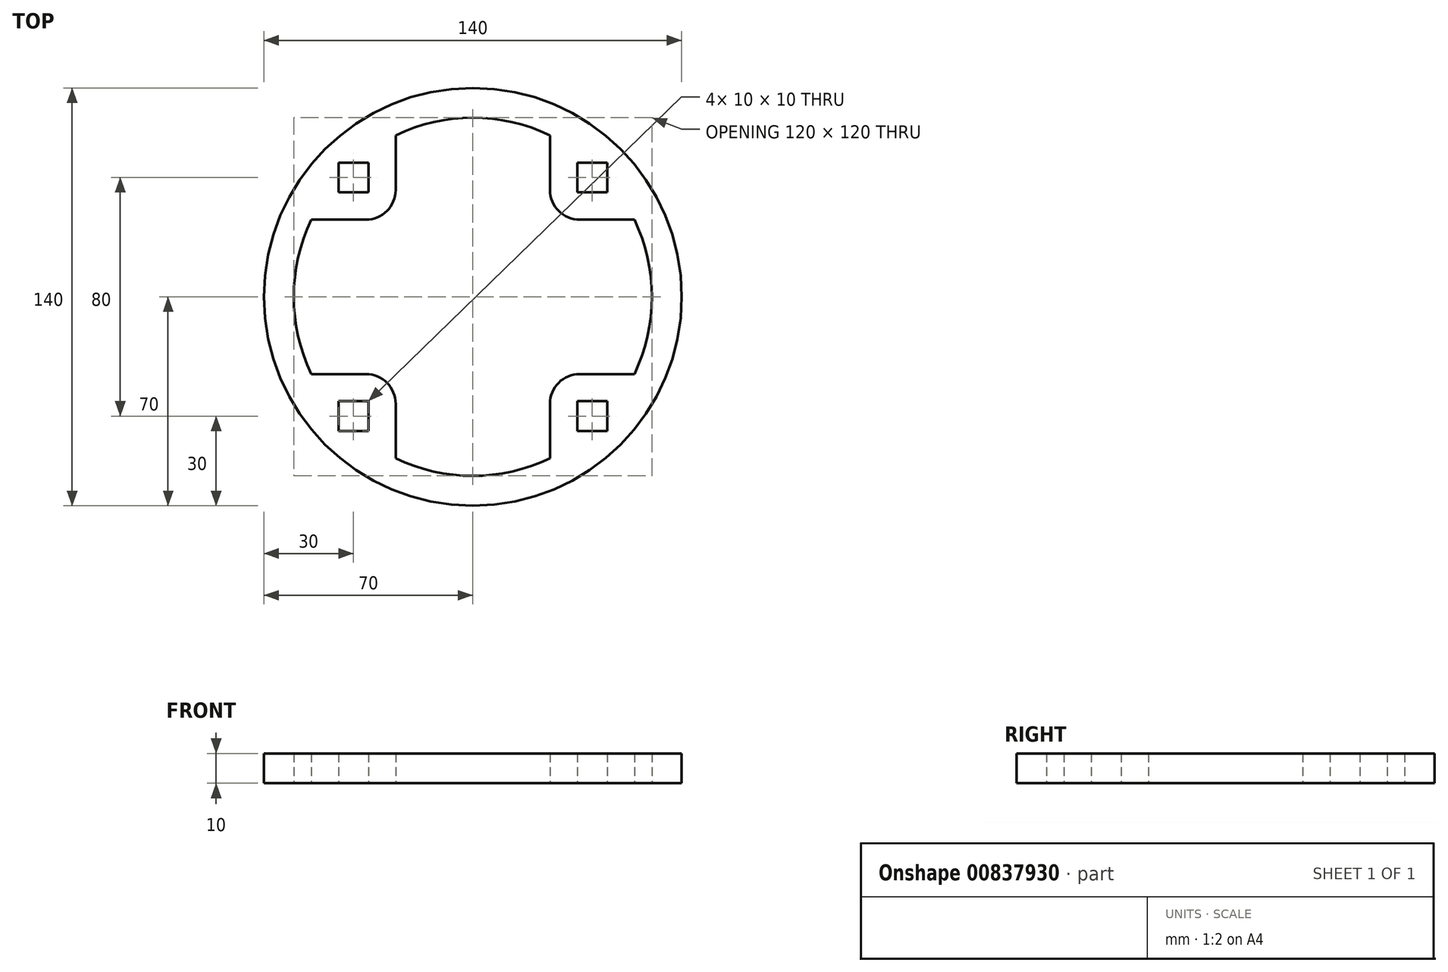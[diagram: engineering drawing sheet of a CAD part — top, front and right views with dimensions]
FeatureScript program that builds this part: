
annotation { "Feature Type Name" : "Feature", "Feature Type Description" : "" }
export const myFeature = defineFeature(function(context is Context, id is Id, definition is map)
    precondition{}
    {
        {
            var Q0;
            Q0=qCreatedBy(makeId("Top.planeOp"),FACE);
            var sketch = newSketch(context, id + "F0", { "sketchPlane" : qUnion([Q0])});
            skCircle(sketch, "E0", {"center": v(0, 0) * mm, "radius": 70 * mm});
            skCircle(sketch, "E1", {"center": v(0, 0) * mm, "radius": 60 * mm});
            skLineSegment(sketch, "E2.bottom", {"start": v(40, 40) * mm, "end": v(-40, 40) * mm});
            skLineSegment(sketch, "E2.top", {"start": v(40, -40) * mm, "end": v(-40, -40) * mm});
            skLineSegment(sketch, "E2.left", {"start": v(40, 40) * mm, "end": v(40, -40) * mm});
            skLineSegment(sketch, "E2.right", {"start": v(-40, 40) * mm, "end": v(-40, -40) * mm});
            skLineSegment(sketch, "E3.bottom", {"start": v(45, 45) * mm, "end": v(35, 45) * mm});
            skLineSegment(sketch, "E3.top", {"start": v(45, 35) * mm, "end": v(35, 35) * mm});
            skLineSegment(sketch, "E3.left", {"start": v(45, 45) * mm, "end": v(45, 35) * mm});
            skLineSegment(sketch, "E3.right", {"start": v(35, 45) * mm, "end": v(35, 35) * mm});
            skPoint(sketch, "E3.middle", {"position": v(40, 40) * mm});
            skLineSegment(sketch, "E4.bottom", {"start": v(54.14, 54.14) * mm, "end": v(25.86, 54.14) * mm});
            skLineSegment(sketch, "E4.top", {"start": v(54.14, 25.86) * mm, "end": v(25.86, 25.86) * mm});
            skLineSegment(sketch, "E4.left", {"start": v(54.14, 54.14) * mm, "end": v(54.14, 25.86) * mm});
            skLineSegment(sketch, "E4.right", {"start": v(25.86, 54.14) * mm, "end": v(25.86, 25.86) * mm});
            skPoint(sketch, "E5.MirrorP", {"position": v(-40, 40) * mm});
            skLineSegment(sketch, "E6.MirrorCS", {"start": v(-45, 45) * mm, "end": v(-45, 35) * mm});
            skLineSegment(sketch, "E7.MirrorCS", {"start": v(-54.14, 54.14) * mm, "end": v(-25.86, 54.14) * mm});
            skLineSegment(sketch, "E8.MirrorCS", {"start": v(-54.14, 54.14) * mm, "end": v(-54.14, 25.86) * mm});
            skLineSegment(sketch, "E9.MirrorCS", {"start": v(-45, 35) * mm, "end": v(-35, 35) * mm});
            skLineSegment(sketch, "E10.MirrorCS", {"start": v(-25.86, 54.14) * mm, "end": v(-25.86, 25.86) * mm});
            skLineSegment(sketch, "E11.MirrorCS", {"start": v(-45, 45) * mm, "end": v(-35, 45) * mm});
            skLineSegment(sketch, "E12.MirrorCS", {"start": v(-54.14, 25.86) * mm, "end": v(-25.86, 25.86) * mm});
            skLineSegment(sketch, "E13.MirrorCS", {"start": v(-35, 45) * mm, "end": v(-35, 35) * mm});
            skLineSegment(sketch, "E14.MirrorCS", {"start": v(-40, 40) * mm, "end": v(40, 40) * mm});
            skPoint(sketch, "E15.MirrorP", {"position": v(-40, -40) * mm});
            skLineSegment(sketch, "E16.MirrorCS", {"start": v(-45, -45) * mm, "end": v(-45, -35) * mm});
            skLineSegment(sketch, "E17.MirrorCS", {"start": v(-54.14, -25.86) * mm, "end": v(-25.86, -25.86) * mm});
            skLineSegment(sketch, "E18.MirrorCS", {"start": v(-54.14, -54.14) * mm, "end": v(-25.86, -54.14) * mm});
            skLineSegment(sketch, "E19.MirrorCS", {"start": v(-45, -35) * mm, "end": v(-35, -35) * mm});
            skLineSegment(sketch, "E20.MirrorCS", {"start": v(-45, -45) * mm, "end": v(-35, -45) * mm});
            skLineSegment(sketch, "E21.MirrorCS", {"start": v(-25.86, -54.14) * mm, "end": v(-25.86, -25.86) * mm});
            skLineSegment(sketch, "E22.MirrorCS", {"start": v(-35, -45) * mm, "end": v(-35, -35) * mm});
            skLineSegment(sketch, "E23.MirrorCS", {"start": v(-54.14, -54.14) * mm, "end": v(-54.14, -25.86) * mm});
            skPoint(sketch, "E24.MirrorP", {"position": v(40, -40) * mm});
            skLineSegment(sketch, "E25.MirrorCS", {"start": v(45, -35) * mm, "end": v(35, -35) * mm});
            skLineSegment(sketch, "E26.MirrorCS", {"start": v(54.14, -25.86) * mm, "end": v(25.86, -25.86) * mm});
            skLineSegment(sketch, "E27.MirrorCS", {"start": v(45, -45) * mm, "end": v(35, -45) * mm});
            skLineSegment(sketch, "E28.MirrorCS", {"start": v(25.86, -54.14) * mm, "end": v(25.86, -25.86) * mm});
            skLineSegment(sketch, "E29.MirrorCS", {"start": v(45, -45) * mm, "end": v(45, -35) * mm});
            skLineSegment(sketch, "E30.MirrorCS", {"start": v(54.14, -54.14) * mm, "end": v(25.86, -54.14) * mm});
            skLineSegment(sketch, "E31.MirrorCS", {"start": v(35, -45) * mm, "end": v(35, -35) * mm});
            skLineSegment(sketch, "E32.MirrorCS", {"start": v(54.14, -54.14) * mm, "end": v(54.14, -25.86) * mm});
            skSolve(sketch);
        }
        {
            var Q0;
            {var subQ0=sQuery(id+"F0.wireOp",EDGE,"E8.MirrorCS");var subQ1=sQuery(id+"F0.wireOp",EDGE,"E0");var subQ2=makeQuery(id+"F0.imprint","INTERSECT",VERTEX,{"derivedFrom":[subQ1,subQ0]});Q0=makeQuery(id+"F0.imprint","IMPRINT",FACE,{"disambiguationData":[TD([[makeQuery(id+"F0.imprint","IMPRINT",EDGE,{"disambiguationData":[TD([[subQ2,-1.0]])],"derivedFrom":subQ1}),1.0]])]});}
            var Q1;
            {var subQ8=sQuery(id+"F0.wireOp",EDGE,"E0");var subQ10=sQuery(id+"F0.wireOp",EDGE,"E7.MirrorCS");var subQ12=makeQuery(id+"F0.imprint","INTERSECT",VERTEX,{"derivedFrom":[subQ8,subQ10]});Q1=makeQuery(id+"F0.imprint","IMPRINT",FACE,{"disambiguationData":[TD([[makeQuery(id+"F0.imprint","IMPRINT",EDGE,{"disambiguationData":[TD([[subQ12,-1.0]])],"derivedFrom":subQ8}),1.0]])]});}
            var Q2;
            {var subQ0=sQuery(id+"F0.wireOp",EDGE,"E4.bottom");var subQ1=sQuery(id+"F0.wireOp",EDGE,"E0");var subQ2=makeQuery(id+"F0.imprint","INTERSECT",VERTEX,{"derivedFrom":[subQ1,subQ0]});Q2=makeQuery(id+"F0.imprint","IMPRINT",FACE,{"disambiguationData":[TD([[makeQuery(id+"F0.imprint","IMPRINT",EDGE,{"disambiguationData":[TD([[subQ2,-1.0]])],"derivedFrom":subQ1}),1.0]])]});}
            var Q3;
            {var subQ3=sQuery(id+"F0.wireOp",EDGE,"E0");var subQ7=sQuery(id+"F0.wireOp",EDGE,"E4.bottom");var subQ9=makeQuery(id+"F0.imprint","INTERSECT",VERTEX,{"derivedFrom":[subQ3,subQ7]});Q3=makeQuery(id+"F0.imprint","IMPRINT",FACE,{"disambiguationData":[TD([[makeQuery(id+"F0.imprint","IMPRINT",EDGE,{"disambiguationData":[TD([[subQ9,1.0]])],"derivedFrom":subQ3}),1.0]])]});}
            var Q4;
            {var subQ0=sQuery(id+"F0.wireOp",EDGE,"E4.left");var subQ1=sQuery(id+"F0.wireOp",EDGE,"E0");var subQ2=makeQuery(id+"F0.imprint","INTERSECT",VERTEX,{"derivedFrom":[subQ1,subQ0]});Q4=makeQuery(id+"F0.imprint","IMPRINT",FACE,{"disambiguationData":[TD([[makeQuery(id+"F0.imprint","IMPRINT",EDGE,{"disambiguationData":[TD([[subQ2,1.0]])],"derivedFrom":subQ1}),1.0]])]});}
            var Q5;
            {var subQ5=sQuery(id+"F0.wireOp",EDGE,"E30.MirrorCS");var subQ10=sQuery(id+"F0.wireOp",EDGE,"E0");var subQ11=makeQuery(id+"F0.imprint","INTERSECT",VERTEX,{"derivedFrom":[subQ10,subQ5]});Q5=makeQuery(id+"F0.imprint","IMPRINT",FACE,{"disambiguationData":[TD([[makeQuery(id+"F0.imprint","IMPRINT",EDGE,{"disambiguationData":[TD([[subQ11,-1.0]])],"derivedFrom":subQ10}),1.0]])]});}
            var Q6;
            {var subQ0=sQuery(id+"F0.wireOp",EDGE,"E18.MirrorCS");var subQ1=sQuery(id+"F0.wireOp",EDGE,"E0");var subQ2=makeQuery(id+"F0.imprint","INTERSECT",VERTEX,{"derivedFrom":[subQ1,subQ0]});Q6=makeQuery(id+"F0.imprint","IMPRINT",FACE,{"disambiguationData":[TD([[makeQuery(id+"F0.imprint","IMPRINT",EDGE,{"disambiguationData":[TD([[subQ2,-1.0]])],"derivedFrom":subQ1}),1.0]])]});}
            var Q7;
            {var subQ8=sQuery(id+"F0.wireOp",EDGE,"E23.MirrorCS");var subQ10=sQuery(id+"F0.wireOp",EDGE,"E0");var subQ11=makeQuery(id+"F0.imprint","INTERSECT",VERTEX,{"derivedFrom":[subQ10,subQ8]});Q7=makeQuery(id+"F0.imprint","IMPRINT",FACE,{"disambiguationData":[TD([[makeQuery(id+"F0.imprint","IMPRINT",EDGE,{"disambiguationData":[TD([[subQ11,-1.0]])],"derivedFrom":subQ10}),1.0]])]});}
            var Q8;
            {var subQ0=sQuery(id+"F0.wireOp",EDGE,"E21.MirrorCS");var subQ8=sQuery(id+"F0.wireOp",EDGE,"E2.top");var subQ11=makeQuery(id+"F0.imprint","INTERSECT",VERTEX,{"derivedFrom":[subQ8,subQ0]});Q8=makeQuery(id+"F0.imprint","IMPRINT",FACE,{"disambiguationData":[TD([[makeQuery(id+"F0.imprint","IMPRINT",EDGE,{"disambiguationData":[TD([[subQ11,-1.0]])],"derivedFrom":subQ8}),-1.0]])]});}
            var Q9;
            {var subQ0=sQuery(id+"F0.wireOp",EDGE,"E17.MirrorCS");var subQ3=sQuery(id+"F0.wireOp",EDGE,"E2.right");var subQ4=makeQuery(id+"F0.imprint","INTERSECT",VERTEX,{"derivedFrom":[subQ3,subQ0]});Q9=makeQuery(id+"F0.imprint","IMPRINT",FACE,{"disambiguationData":[TD([[makeQuery(id+"F0.imprint","IMPRINT",EDGE,{"disambiguationData":[TD([[subQ4,-1.0]])],"derivedFrom":subQ3}),-1.0]])]});}
            var Q10;
            {var subQ5=sQuery(id+"F0.wireOp",EDGE,"E2.top");var subQ7=sQuery(id+"F0.wireOp",EDGE,"E21.MirrorCS");var subQ8=makeQuery(id+"F0.imprint","INTERSECT",VERTEX,{"derivedFrom":[subQ5,subQ7]});Q10=makeQuery(id+"F0.imprint","IMPRINT",FACE,{"disambiguationData":[TD([[makeQuery(id+"F0.imprint","IMPRINT",EDGE,{"disambiguationData":[TD([[subQ8,-1.0]])],"derivedFrom":subQ5}),1.0]])]});}
            var Q11;
            {var subQ0=sQuery(id+"F0.wireOp",EDGE,"E31.MirrorCS");var subQ7=sQuery(id+"F0.wireOp",EDGE,"E2.top");var subQ9=makeQuery(id+"F0.imprint","INTERSECT",VERTEX,{"derivedFrom":[subQ7,subQ0]});Q11=makeQuery(id+"F0.imprint","IMPRINT",FACE,{"disambiguationData":[TD([[makeQuery(id+"F0.imprint","IMPRINT",EDGE,{"disambiguationData":[TD([[subQ9,-1.0]])],"derivedFrom":subQ7}),1.0]])]});}
            var Q12;
            {var subQ7=sQuery(id+"F0.wireOp",EDGE,"E2.top");var subQ9=sQuery(id+"F0.wireOp",EDGE,"E31.MirrorCS");var subQ10=makeQuery(id+"F0.imprint","INTERSECT",VERTEX,{"derivedFrom":[subQ7,subQ9]});Q12=makeQuery(id+"F0.imprint","IMPRINT",FACE,{"disambiguationData":[TD([[makeQuery(id+"F0.imprint","IMPRINT",EDGE,{"disambiguationData":[TD([[subQ10,-1.0]])],"derivedFrom":subQ7}),-1.0]])]});}
            var Q13;
            {var subQ5=sQuery(id+"F0.wireOp",EDGE,"E26.MirrorCS");var subQ7=sQuery(id+"F0.wireOp",EDGE,"E2.left");var subQ8=makeQuery(id+"F0.imprint","INTERSECT",VERTEX,{"derivedFrom":[subQ7,subQ5]});Q13=makeQuery(id+"F0.imprint","IMPRINT",FACE,{"disambiguationData":[TD([[makeQuery(id+"F0.imprint","IMPRINT",EDGE,{"disambiguationData":[TD([[subQ8,-1.0]])],"derivedFrom":subQ7}),1.0]])]});}
            var Q14;
            {var subQ1=sQuery(id+"F0.wireOp",EDGE,"E3.top");var subQ5=sQuery(id+"F0.wireOp",EDGE,"E2.left");var subQ6=makeQuery(id+"F0.imprint","INTERSECT",VERTEX,{"derivedFrom":[subQ5,subQ1]});Q14=makeQuery(id+"F0.imprint","IMPRINT",FACE,{"disambiguationData":[TD([[makeQuery(id+"F0.imprint","IMPRINT",EDGE,{"disambiguationData":[TD([[subQ6,-1.0]])],"derivedFrom":subQ5}),1.0]])]});}
            var Q15;
            {var subQ6=sQuery(id+"F0.wireOp",EDGE,"E3.top");var subQ8=sQuery(id+"F0.wireOp",EDGE,"E2.left");var subQ9=makeQuery(id+"F0.imprint","INTERSECT",VERTEX,{"derivedFrom":[subQ8,subQ6]});Q15=makeQuery(id+"F0.imprint","IMPRINT",FACE,{"disambiguationData":[TD([[makeQuery(id+"F0.imprint","IMPRINT",EDGE,{"disambiguationData":[TD([[subQ9,-1.0]])],"derivedFrom":subQ8}),-1.0]])]});}
            var Q16;
            {var subQ0=sQuery(id+"F0.wireOp",EDGE,"E3.right");var subQ7=sQuery(id+"F0.wireOp",EDGE,"E2.bottom");var subQ9=makeQuery(id+"F0.imprint","INTERSECT",VERTEX,{"derivedFrom":[subQ7,subQ0]});Q16=makeQuery(id+"F0.imprint","IMPRINT",FACE,{"disambiguationData":[TD([[makeQuery(id+"F0.imprint","IMPRINT",EDGE,{"disambiguationData":[TD([[subQ9,-1.0]])],"derivedFrom":subQ7}),-1.0]])]});}
            var Q17;
            {var subQ5=sQuery(id+"F0.wireOp",EDGE,"E13.MirrorCS");var subQ7=sQuery(id+"F0.wireOp",EDGE,"E11.MirrorCS");var subQ8=makeQuery(id+"F0.imprint","INTERSECT",VERTEX,{"derivedFrom":[subQ5,subQ7]});Q17=makeQuery(id+"F0.imprint","IMPRINT",FACE,{"disambiguationData":[TD([[makeQuery(id+"F0.imprint","IMPRINT",EDGE,{"disambiguationData":[TD([[subQ8,-1.0]])],"derivedFrom":subQ5}),1.0]])]});}
            var Q18;
            {var subQ0=sQuery(id+"F0.wireOp",EDGE,"E9.MirrorCS");var subQ8=sQuery(id+"F0.wireOp",EDGE,"E2.right");var subQ11=makeQuery(id+"F0.imprint","INTERSECT",VERTEX,{"derivedFrom":[subQ8,subQ0]});Q18=makeQuery(id+"F0.imprint","IMPRINT",FACE,{"disambiguationData":[TD([[makeQuery(id+"F0.imprint","IMPRINT",EDGE,{"disambiguationData":[TD([[subQ11,-1.0]])],"derivedFrom":subQ8}),1.0]])]});}
            var Q19;
            {var subQ3=sQuery(id+"F0.wireOp",EDGE,"E2.right");var subQ5=sQuery(id+"F0.wireOp",EDGE,"E9.MirrorCS");var subQ9=makeQuery(id+"F0.imprint","INTERSECT",VERTEX,{"derivedFrom":[subQ3,subQ5]});Q19=makeQuery(id+"F0.imprint","IMPRINT",FACE,{"disambiguationData":[TD([[makeQuery(id+"F0.imprint","IMPRINT",EDGE,{"disambiguationData":[TD([[subQ9,-1.0]])],"derivedFrom":subQ3}),-1.0]])]});}
            extrude(context, id + "F1", {"entities" : qUnion([Q0, Q1, Q2, Q3, Q4, Q5, Q6, Q7, Q8, Q9, Q10, Q11, Q12, Q13, Q14, Q15, Q16, Q17, Q18, Q19]), "depth" : 10 * mm, "offsetDistance" : 25 * mm});
        }
        {
            var Q0;
            Q0=makeQuery(id+"F1.opExtrude","SWEPT_EDGE",EDGE,{"disambiguationData":[OSD([sQuery(id+"F0.wireOp",EDGE,"E4.right"),sQuery(id+"F0.wireOp",EDGE,"E4.top")])]});
            var Q1;
            Q1=makeQuery(id+"F1.opExtrude","SWEPT_EDGE",EDGE,{"disambiguationData":[OSD([sQuery(id+"F0.wireOp",EDGE,"E26.MirrorCS"),sQuery(id+"F0.wireOp",EDGE,"E28.MirrorCS")])]});
            var Q2;
            Q2=makeQuery(id+"F1.opExtrude","SWEPT_EDGE",EDGE,{"disambiguationData":[OSD([sQuery(id+"F0.wireOp",EDGE,"E10.MirrorCS"),sQuery(id+"F0.wireOp",EDGE,"E12.MirrorCS")])]});
            var Q3;
            Q3=makeQuery(id+"F1.opExtrude","SWEPT_EDGE",EDGE,{"disambiguationData":[OSD([sQuery(id+"F0.wireOp",EDGE,"E17.MirrorCS"),sQuery(id+"F0.wireOp",EDGE,"E21.MirrorCS")])]});
            fillet(context, id + "F2", {"entities" : qUnion([Q0, Q1, Q2, Q3]), "radius" : 10 * mm, "tangentPropagation" : true, "allowEdgeOverflow" : false});
        }
    });
